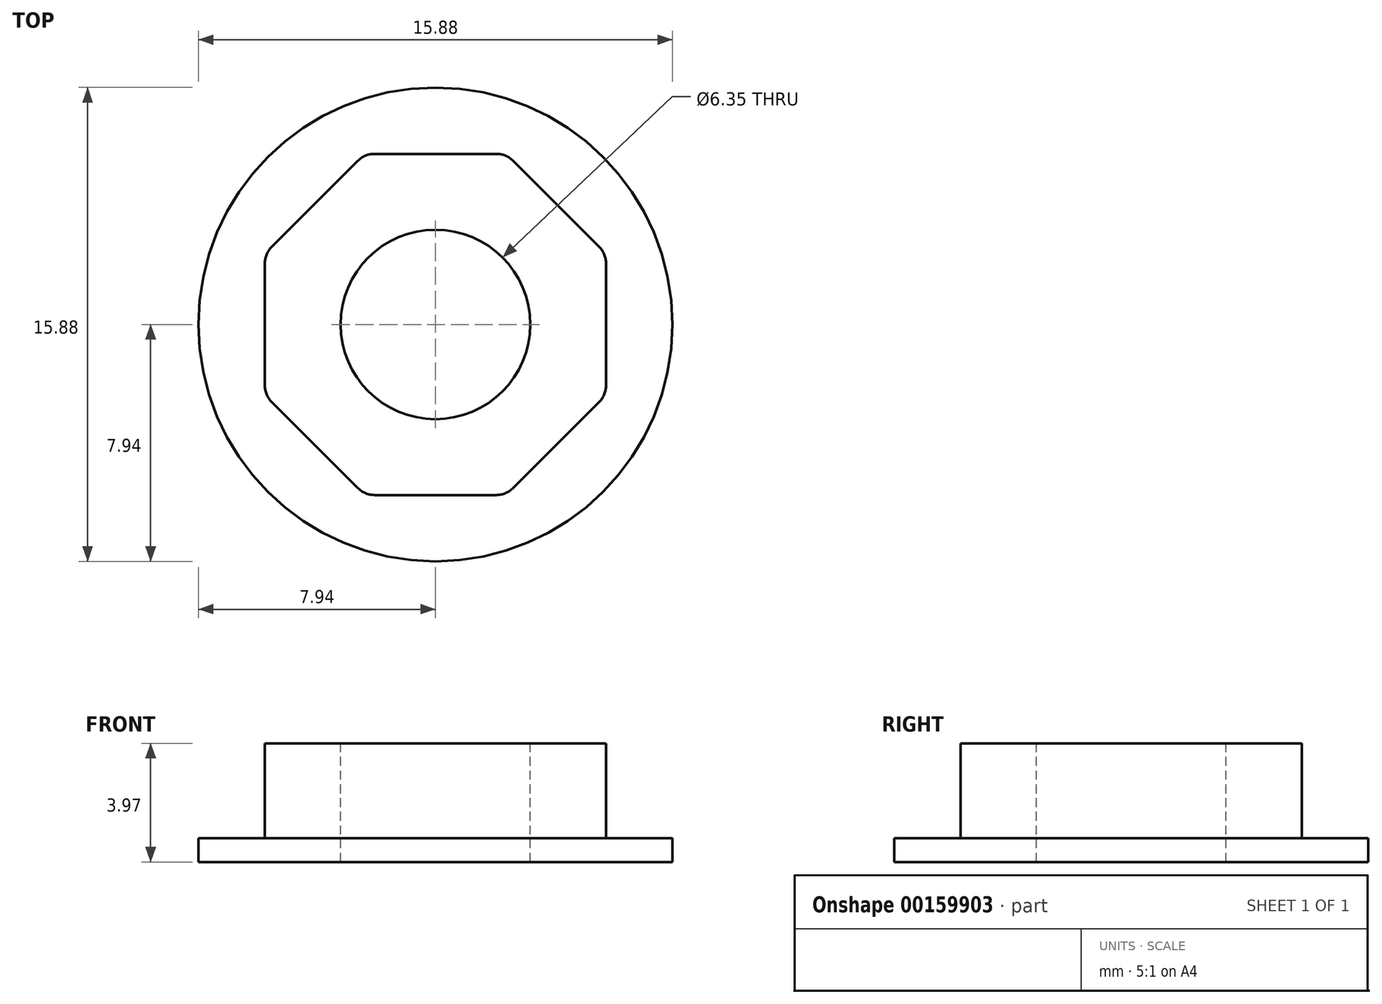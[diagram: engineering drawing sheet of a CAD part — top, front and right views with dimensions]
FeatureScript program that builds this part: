
annotation { "Feature Type Name" : "Feature", "Feature Type Description" : "" }
export const myFeature = defineFeature(function(context is Context, id is Id, definition is map)
    precondition{}
    {
        {
            var Q0;
            Q0=qCreatedBy(makeId("Top.planeOp"),FACE);
            var sketch = newSketch(context, id + "F0", { "sketchPlane" : qUnion([Q0])});
            skCircle(sketch, "E0", {"center": v(0, 0) * mm, "radius": 7.94 * mm});
            skSolve(sketch);
        }
        {
            var Q0;
            Q0=makeQuery(id+"F0.imprint","IMPRINT",FACE,{"disambiguationData":[TD([[makeQuery(id+"F0.imprint","IMPRINT",EDGE,{"derivedFrom":sQuery(id+"F0.wireOp",EDGE,"E0")}),1.0]])]});
            extrude(context, id + "F1", {"entities" : qUnion([Q0]), "depth" : 0.8 * mm});
        }
        {
            var Q0;
            Q0=makeQuery(id+"F1.opExtrude","CAP_FACE",FACE,{"disambiguationData":[OSD([sQuery(id+"F0.wireOp",EDGE,"E0")])],"isStart":false});
            var sketch = newSketch(context, id + "F2", { "sketchPlane" : qUnion([Q0])});
            skPoint(sketch, "E1.middle", {"position": v(0, 0) * mm});
            skLineSegment(sketch, "E2", {"start": v(-5.72, 0) * mm, "end": v(5.71, 0) * mm, "construction": true});
            skLineSegment(sketch, "E3", {"start": v(0, -5.72) * mm, "end": v(0, 5.72) * mm, "construction": true});
            skLineSegment(sketch, "E4", {"start": v(-5.71, -2.37) * mm, "end": v(-5.72, 2.37) * mm});
            skLineSegment(sketch, "E5", {"start": v(-5.72, 2.37) * mm, "end": v(-2.37, 5.72) * mm});
            skLineSegment(sketch, "E6", {"start": v(-2.37, 5.72) * mm, "end": v(2.37, 5.72) * mm});
            skLineSegment(sketch, "E7", {"start": v(2.37, 5.71) * mm, "end": v(5.72, 2.37) * mm});
            skLineSegment(sketch, "E8", {"start": v(5.71, 2.37) * mm, "end": v(5.71, -2.37) * mm});
            skLineSegment(sketch, "E9", {"start": v(5.72, -2.37) * mm, "end": v(2.37, -5.72) * mm});
            skLineSegment(sketch, "E10", {"start": v(2.37, -5.72) * mm, "end": v(-2.37, -5.72) * mm});
            skLineSegment(sketch, "E11", {"start": v(-2.37, -5.72) * mm, "end": v(-5.72, -2.37) * mm});
            skSolve(sketch);
        }
        {
            var Q0;
            Q0=makeQuery(id+"F2.imprint","IMPRINT",FACE,{"disambiguationData":[TD([[makeQuery(id+"F2.imprint","IMPRINT",EDGE,{"derivedFrom":sQuery(id+"F2.wireOp",EDGE,"E4")}),-1.0]])]});
            extrude(context, id + "F3", {"entities" : qUnion([Q0]), "operationType" : NewBodyOperationType.ADD, "depth" : 3.17 * mm});
        }
        {
            var Q0;
            Q0=makeQuery(id+"F3.opExtrude","SWEPT_EDGE",EDGE,{"disambiguationData":[OSD([sQuery(id+"F2.wireOp",EDGE,"E4"),sQuery(id+"F2.wireOp",EDGE,"E11")])]});
            var Q1;
            Q1=makeQuery(id+"F3.opExtrude","SWEPT_EDGE",EDGE,{"disambiguationData":[OSD([sQuery(id+"F2.wireOp",EDGE,"E10"),sQuery(id+"F2.wireOp",EDGE,"E11")])]});
            var Q2;
            Q2=makeQuery(id+"F3.opExtrude","SWEPT_EDGE",EDGE,{"disambiguationData":[OSD([sQuery(id+"F2.wireOp",EDGE,"E9"),sQuery(id+"F2.wireOp",EDGE,"E10")])]});
            var Q3;
            Q3=makeQuery(id+"F3.opExtrude","SWEPT_EDGE",EDGE,{"disambiguationData":[OSD([sQuery(id+"F2.wireOp",EDGE,"E8"),sQuery(id+"F2.wireOp",EDGE,"E9")])]});
            var Q4;
            Q4=makeQuery(id+"F3.opExtrude","SWEPT_EDGE",EDGE,{"disambiguationData":[OSD([sQuery(id+"F2.wireOp",EDGE,"E7"),sQuery(id+"F2.wireOp",EDGE,"E8")])]});
            var Q5;
            Q5=makeQuery(id+"F3.opExtrude","SWEPT_EDGE",EDGE,{"disambiguationData":[OSD([sQuery(id+"F2.wireOp",EDGE,"E6"),sQuery(id+"F2.wireOp",EDGE,"E7")])]});
            var Q6;
            Q6=makeQuery(id+"F3.opExtrude","SWEPT_EDGE",EDGE,{"disambiguationData":[OSD([sQuery(id+"F2.wireOp",EDGE,"E5"),sQuery(id+"F2.wireOp",EDGE,"E6")])]});
            var Q7;
            Q7=makeQuery(id+"F3.opExtrude","SWEPT_EDGE",EDGE,{"disambiguationData":[OSD([sQuery(id+"F2.wireOp",EDGE,"E4"),sQuery(id+"F2.wireOp",EDGE,"E5")])]});
            var Q8;
            Q8=makeQuery(id+"F3.opExtrude","CAP_EDGE",EDGE,{"disambiguationData":[OSD([sQuery(id+"F2.wireOp",EDGE,"E5")])],"isStart":true});
            var Q9;
            Q9=makeQuery(id+"F3.opExtrude","CAP_EDGE",EDGE,{"disambiguationData":[OSD([sQuery(id+"F2.wireOp",EDGE,"E6")])],"isStart":true});
            fillet(context, id + "F4", {"entities" : qUnion([Q0, Q1, Q2, Q3, Q4, Q5, Q6, Q7, Q8, Q9]), "radius" : 0.8 * mm, "tangentPropagation" : true, "allowEdgeOverflow" : false});
        }
        {
            var Q0;
            Q0=makeQuery(id+"F3.opExtrude","CAP_FACE",FACE,{"disambiguationData":[OSD([sQuery(id+"F2.wireOp",EDGE,"E4"),sQuery(id+"F2.wireOp",EDGE,"E5"),sQuery(id+"F2.wireOp",EDGE,"E6"),sQuery(id+"F2.wireOp",EDGE,"E7"),sQuery(id+"F2.wireOp",EDGE,"E8"),sQuery(id+"F2.wireOp",EDGE,"E9"),sQuery(id+"F2.wireOp",EDGE,"E10"),sQuery(id+"F2.wireOp",EDGE,"E11")])],"isStart":false});
            var sketch = newSketch(context, id + "F5", { "sketchPlane" : qUnion([Q0])});
            skPoint(sketch, "E12", {"position": v(0, 0) * mm});
            skSolve(sketch);
        }
        {
            var Q0;
            Q0=sQuery(id+"F5.wireOp",VERTEX,"E12");
            var Q1;
            Q1=makeQuery(id+"F1.opExtrude","SWEPT_BODY",BODY,{"disambiguationData":[OSD([sQuery(id+"F0.wireOp",EDGE,"E0")])]});
            hole(context, id + "F6", {"style" : HoleStyle.SIMPLE, "endStyle" : HoleEndStyle.BLIND, "holeDiameter" : 6.35 * mm, "holeDepth" : 19.05 * mm, "locations" : qUnion([Q0]), "scope" : qUnion([Q1])});
        }
    });
